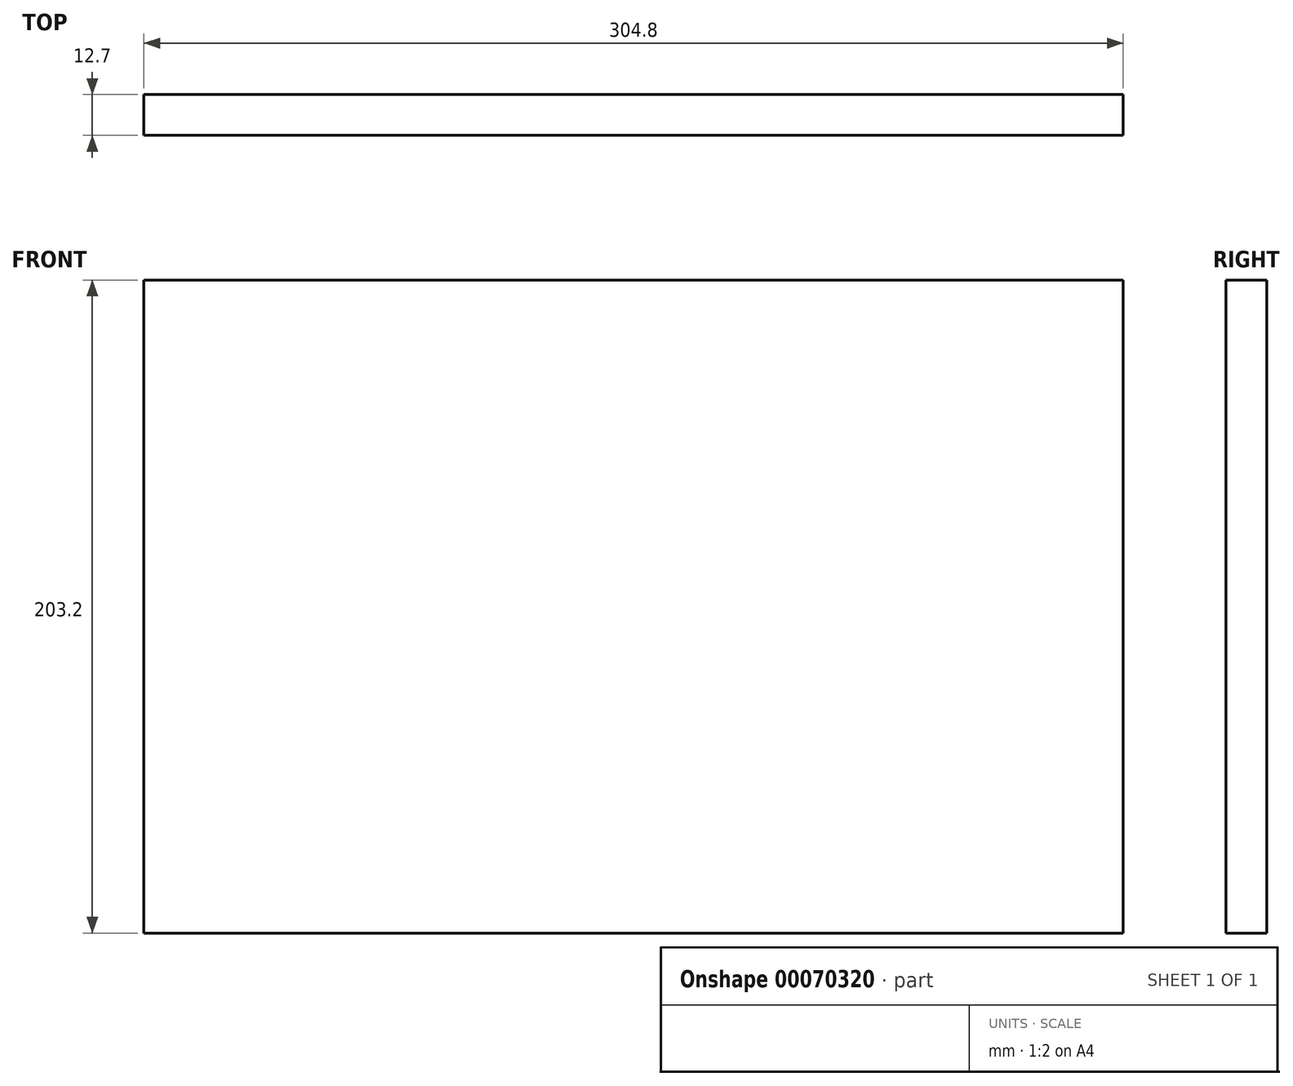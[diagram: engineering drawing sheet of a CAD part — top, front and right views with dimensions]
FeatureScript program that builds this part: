
annotation { "Feature Type Name" : "Feature", "Feature Type Description" : "" }
export const myFeature = defineFeature(function(context is Context, id is Id, definition is map)
    precondition{}
    {
        {
            var Q0;
            Q0=qCreatedBy(makeId("Front.planeOp"),FACE);
            var sketch = newSketch(context, id + "F0", { "sketchPlane" : qUnion([Q0])});
            skLineSegment(sketch, "E0.rect.bottom", {"start": v(152.4, -101.6) * mm, "end": v(-152.4, -101.6) * mm});
            skLineSegment(sketch, "E0.rect.top", {"start": v(152.4, 101.6) * mm, "end": v(-152.4, 101.6) * mm});
            skLineSegment(sketch, "E0.rect.left", {"start": v(152.4, -101.6) * mm, "end": v(152.4, 101.6) * mm});
            skLineSegment(sketch, "E0.rect.right", {"start": v(-152.4, -101.6) * mm, "end": v(-152.4, 101.6) * mm});
            skPoint(sketch, "E0.rect.middle", {"position": v(0, 0) * mm});
            skSolve(sketch);
        }
        {
            var Q0;
            Q0 = qSketchRegion(id + "F0", true);
            extrude(context, id + "F1", {"entities" : qUnion([Q0]), "oppositeDirection" : true, "depth" : 12.7 * mm});
        }
    });
